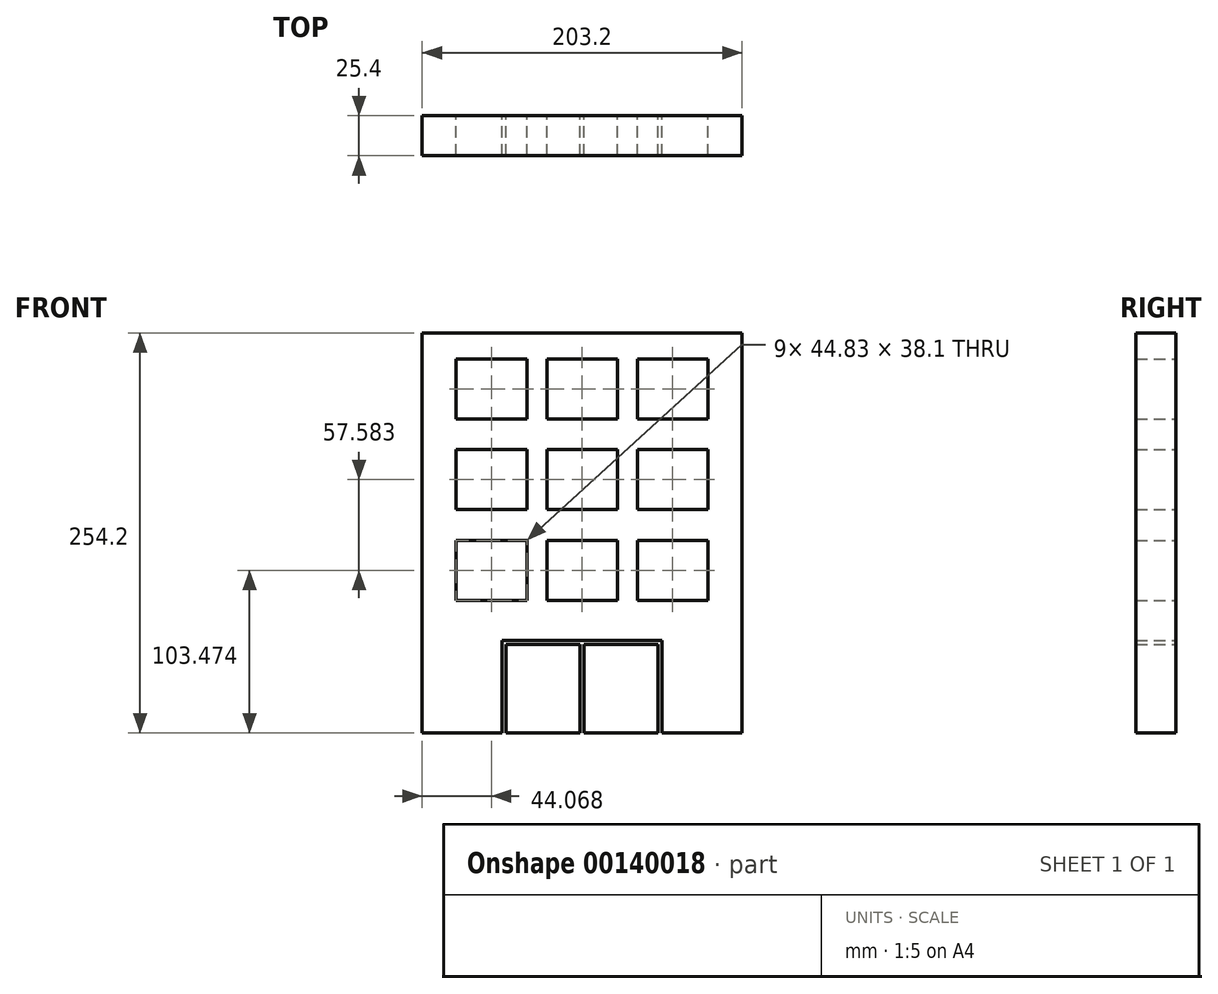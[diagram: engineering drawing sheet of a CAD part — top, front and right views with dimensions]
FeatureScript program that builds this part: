
annotation { "Feature Type Name" : "Feature", "Feature Type Description" : "" }
export const myFeature = defineFeature(function(context is Context, id is Id, definition is map)
    precondition{}
    {
        {
            var Q0;
            Q0=qCreatedBy(makeId("Front.planeOp"),FACE);
            var sketch = newSketch(context, id + "F0", { "sketchPlane" : qUnion([Q0])});
            skLineSegment(sketch, "E0.bottom", {"start": v(-101.6, 127) * mm, "end": v(101.6, 127) * mm});
            skLineSegment(sketch, "E0.left", {"start": v(-101.6, 127) * mm, "end": v(-101.6, -127) * mm});
            skLineSegment(sketch, "E0.right", {"start": v(101.6, 127) * mm, "end": v(101.6, -127) * mm});
            skPoint(sketch, "E0.middle", {"position": v(0, 0) * mm});
            skLineSegment(sketch, "E1.bottom", {"start": v(-79.95, 110.49) * mm, "end": v(-35.12, 110.49) * mm});
            skLineSegment(sketch, "E1.top", {"start": v(-79.95, 72.39) * mm, "end": v(-35.12, 72.39) * mm});
            skLineSegment(sketch, "E1.left", {"start": v(-79.95, 110.49) * mm, "end": v(-79.95, 72.39) * mm});
            skLineSegment(sketch, "E1.right", {"start": v(-35.12, 110.49) * mm, "end": v(-35.12, 72.39) * mm});
            skLineSegment(sketch, "E2.0.1.0", {"start": v(-79.95, 14.8) * mm, "end": v(-35.12, 14.8) * mm});
            skLineSegment(sketch, "E2.0.1.1", {"start": v(-35.12, 52.9) * mm, "end": v(-35.12, 14.8) * mm});
            skLineSegment(sketch, "E2.0.1.2", {"start": v(-79.95, 52.9) * mm, "end": v(-35.12, 52.9) * mm});
            skLineSegment(sketch, "E2.0.1.3", {"start": v(-79.95, 52.9) * mm, "end": v(-79.95, 14.8) * mm});
            skLineSegment(sketch, "E2.0.2.0", {"start": v(-79.95, -42.78) * mm, "end": v(-35.12, -42.78) * mm});
            skLineSegment(sketch, "E2.0.2.1", {"start": v(-35.12, -4.68) * mm, "end": v(-35.12, -42.78) * mm});
            skLineSegment(sketch, "E2.0.2.2", {"start": v(-79.95, -4.68) * mm, "end": v(-35.12, -4.68) * mm});
            skLineSegment(sketch, "E2.0.2.3", {"start": v(-79.95, -4.68) * mm, "end": v(-79.95, -42.78) * mm});
            skLineSegment(sketch, "E2.1.0.0", {"start": v(-22.42, 72.39) * mm, "end": v(22.42, 72.39) * mm});
            skLineSegment(sketch, "E2.1.0.1", {"start": v(22.42, 110.49) * mm, "end": v(22.42, 72.39) * mm});
            skLineSegment(sketch, "E2.1.0.2", {"start": v(-22.42, 110.49) * mm, "end": v(22.42, 110.49) * mm});
            skLineSegment(sketch, "E2.1.0.3", {"start": v(-22.42, 110.49) * mm, "end": v(-22.42, 72.39) * mm});
            skLineSegment(sketch, "E2.1.1.0", {"start": v(-22.42, 14.8) * mm, "end": v(22.42, 14.8) * mm});
            skLineSegment(sketch, "E2.1.1.1", {"start": v(22.42, 52.9) * mm, "end": v(22.42, 14.8) * mm});
            skLineSegment(sketch, "E2.1.1.2", {"start": v(-22.42, 52.9) * mm, "end": v(22.42, 52.9) * mm});
            skLineSegment(sketch, "E2.1.1.3", {"start": v(-22.42, 52.9) * mm, "end": v(-22.42, 14.8) * mm});
            skLineSegment(sketch, "E2.1.2.0", {"start": v(-22.42, -42.78) * mm, "end": v(22.42, -42.78) * mm});
            skLineSegment(sketch, "E2.1.2.1", {"start": v(22.42, -4.68) * mm, "end": v(22.42, -42.78) * mm});
            skLineSegment(sketch, "E2.1.2.2", {"start": v(-22.42, -4.68) * mm, "end": v(22.42, -4.68) * mm});
            skLineSegment(sketch, "E2.1.2.3", {"start": v(-22.42, -4.68) * mm, "end": v(-22.42, -42.78) * mm});
            skLineSegment(sketch, "E2.2.0.0", {"start": v(35.12, 72.39) * mm, "end": v(79.95, 72.39) * mm});
            skLineSegment(sketch, "E2.2.0.1", {"start": v(79.95, 110.49) * mm, "end": v(79.95, 72.39) * mm});
            skLineSegment(sketch, "E2.2.0.2", {"start": v(35.12, 110.49) * mm, "end": v(79.95, 110.49) * mm});
            skLineSegment(sketch, "E2.2.0.3", {"start": v(35.12, 110.49) * mm, "end": v(35.12, 72.39) * mm});
            skLineSegment(sketch, "E2.2.1.0", {"start": v(35.12, 14.8) * mm, "end": v(79.95, 14.8) * mm});
            skLineSegment(sketch, "E2.2.1.1", {"start": v(79.95, 52.9) * mm, "end": v(79.95, 14.8) * mm});
            skLineSegment(sketch, "E2.2.1.2", {"start": v(35.12, 52.9) * mm, "end": v(79.95, 52.9) * mm});
            skLineSegment(sketch, "E2.2.1.3", {"start": v(35.12, 52.9) * mm, "end": v(35.12, 14.8) * mm});
            skLineSegment(sketch, "E2.2.2.0", {"start": v(35.12, -42.78) * mm, "end": v(79.95, -42.78) * mm});
            skLineSegment(sketch, "E2.2.2.1", {"start": v(79.95, -4.68) * mm, "end": v(79.95, -42.78) * mm});
            skLineSegment(sketch, "E2.2.2.2", {"start": v(35.12, -4.68) * mm, "end": v(79.95, -4.68) * mm});
            skLineSegment(sketch, "E2.2.2.3", {"start": v(35.12, -4.68) * mm, "end": v(35.12, -42.78) * mm});
            skLineSegment(sketch, "E2.direction1", {"start": v(-79.95, 72.39) * mm, "end": v(-22.42, 72.39) * mm, "construction": true});
            skLineSegment(sketch, "E2.direction2", {"start": v(-79.95, 72.39) * mm, "end": v(-79.95, 14.8) * mm, "construction": true});
            skPoint(sketch, "E3", {"position": v(0, 127) * mm});
            skPoint(sketch, "E4", {"position": v(0, 110.49) * mm});
            skLineSegment(sketch, "E5.top", {"start": v(-50.8, -68.28) * mm, "end": v(50.8, -68.28) * mm});
            skLineSegment(sketch, "E5.left", {"start": v(-50.8, -127.55) * mm, "end": v(-50.8, -68.28) * mm});
            skLineSegment(sketch, "E5.right", {"start": v(50.8, -127) * mm, "end": v(50.8, -68.28) * mm});
            skLineSegment(sketch, "E6", {"start": v(-101.6, -127) * mm, "end": v(-50.8, -127) * mm});
            skPoint(sketch, "E7", {"position": v(0, -68.28) * mm});
            skLineSegment(sketch, "E8.trimOffspring", {"start": v(50.8, -127) * mm, "end": v(101.6, -127) * mm});
            skLineSegment(sketch, "E9.bottom", {"start": v(-48.26, -127.2) * mm, "end": v(-1.27, -127.2) * mm});
            skLineSegment(sketch, "E9.top", {"start": v(-48.26, -70.82) * mm, "end": v(-1.27, -70.82) * mm});
            skLineSegment(sketch, "E9.left", {"start": v(-48.26, -127.2) * mm, "end": v(-48.26, -70.82) * mm});
            skLineSegment(sketch, "E9.right", {"start": v(48.26, -127.2) * mm, "end": v(48.26, -70.82) * mm});
            skLineSegment(sketch, "E10", {"start": v(-1.27, -70.82) * mm, "end": v(-1.27, -127) * mm});
            skLineSegment(sketch, "E11", {"start": v(0, -68.28) * mm, "end": v(0, -127.2) * mm, "construction": true});
            skLineSegment(sketch, "E12.MirrorCS", {"start": v(1.27, -70.82) * mm, "end": v(1.27, -127) * mm});
            skLineSegment(sketch, "E13.trimOffspring", {"start": v(1.27, -70.82) * mm, "end": v(48.26, -70.82) * mm});
            skLineSegment(sketch, "E14", {"start": v(-1.27, -127) * mm, "end": v(-1.27, -127.2) * mm});
            skLineSegment(sketch, "E15", {"start": v(1.27, -127) * mm, "end": v(1.27, -127.2) * mm});
            skLineSegment(sketch, "E16.trimOffspring", {"start": v(1.27, -127.2) * mm, "end": v(48.26, -127.2) * mm});
            skSolve(sketch);
        }
        {
            var Q0;
            Q0=makeQuery(id+"F0.imprint","IMPRINT",FACE,{"disambiguationData":[TD([[makeQuery(id+"F0.imprint","IMPRINT",EDGE,{"derivedFrom":sQuery(id+"F0.wireOp",EDGE,"E0.bottom")}),-1.0]])]});
            var Q1;
            Q1=makeQuery(id+"F0.imprint","IMPRINT",FACE,{"disambiguationData":[TD([[makeQuery(id+"F0.imprint","IMPRINT",EDGE,{"derivedFrom":sQuery(id+"F0.wireOp",EDGE,"E9.bottom")}),1.0]])]});
            var Q2;
            Q2=makeQuery(id+"F0.imprint","IMPRINT",FACE,{"disambiguationData":[TD([[makeQuery(id+"F0.imprint","IMPRINT",EDGE,{"derivedFrom":sQuery(id+"F0.wireOp",EDGE,"E9.right")}),1.0]])]});
            extrude(context, id + "F1", {"entities" : qUnion([Q0, Q1, Q2]), "depth" : 25.4 * mm});
        }
    });
